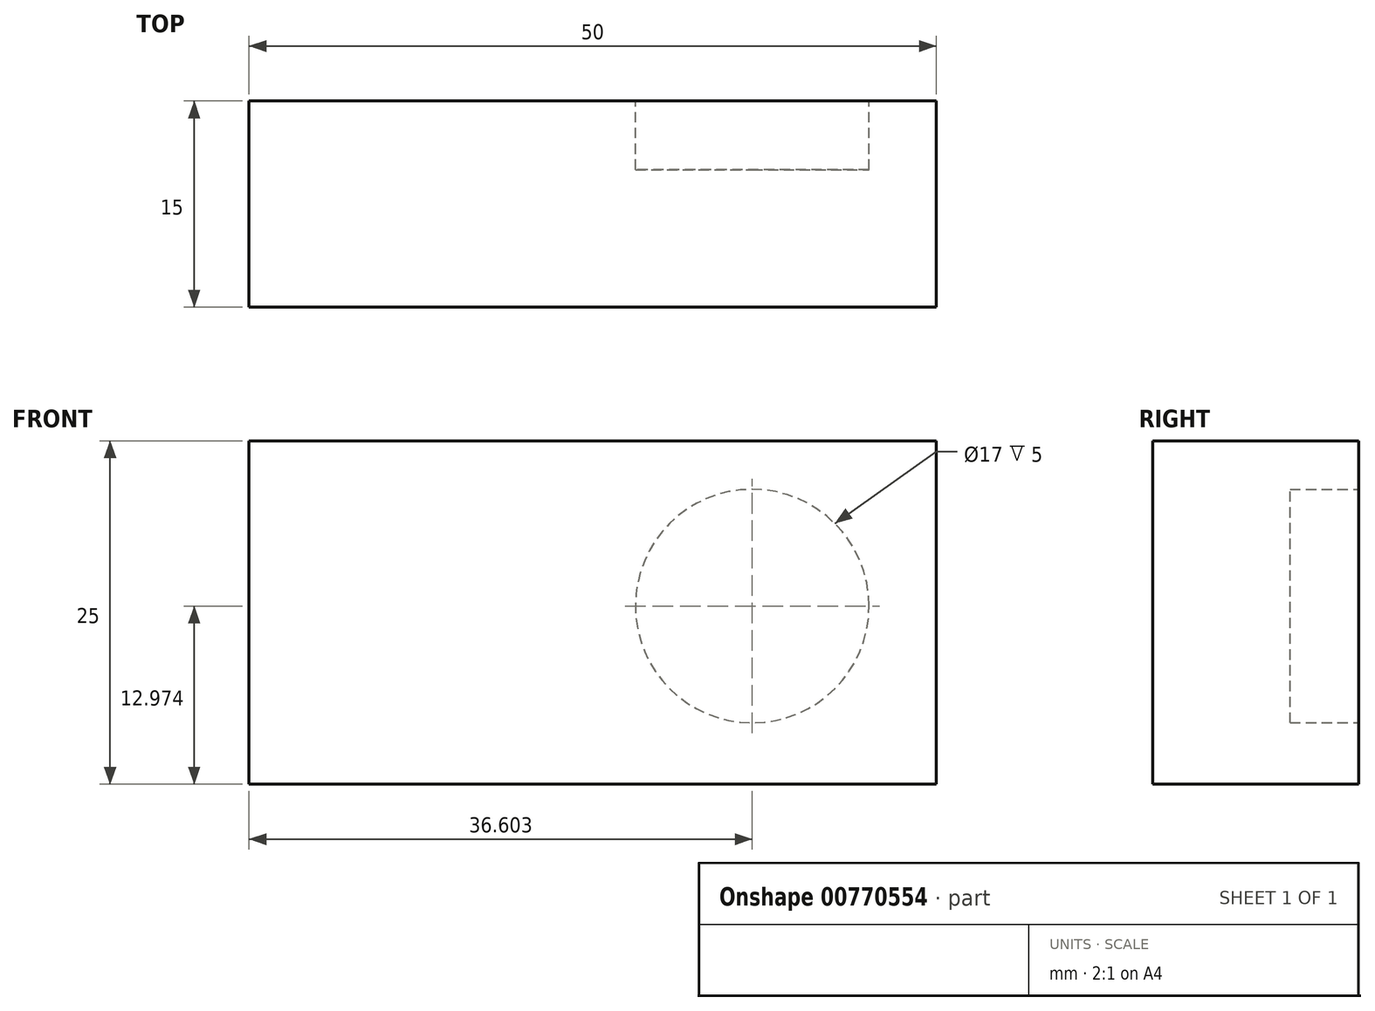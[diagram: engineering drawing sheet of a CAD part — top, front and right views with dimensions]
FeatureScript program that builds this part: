
annotation { "Feature Type Name" : "Feature", "Feature Type Description" : "" }
export const myFeature = defineFeature(function(context is Context, id is Id, definition is map)
    precondition{}
    {
        {
            var Q0;
            Q0=qCreatedBy(makeId("Front.planeOp"),FACE);
            var sketch = newSketch(context, id + "F0", { "sketchPlane" : qUnion([Q0])});
            skLineSegment(sketch, "E0.bottom", {"start": v(0, 0) * mm, "end": v(-50, 0) * mm});
            skLineSegment(sketch, "E0.top", {"start": v(0, 25) * mm, "end": v(-50, 25) * mm});
            skLineSegment(sketch, "E0.left", {"start": v(0, 0) * mm, "end": v(0, 25) * mm});
            skLineSegment(sketch, "E0.right", {"start": v(-50, 0) * mm, "end": v(-50, 25) * mm});
            skSolve(sketch);
        }
        {
            var Q0;
            Q0=qCreatedBy(makeId("Front.planeOp"),FACE);
            var sketch = newSketch(context, id + "F1", { "sketchPlane" : qUnion([Q0])});
            skCircle(sketch, "E1", {"center": v(-13.4, 12.97) * mm, "radius": 8.5 * mm});
            skSolve(sketch);
        }
        {
            var Q0;
            Q0 = qSketchRegion(id + "F0", true);
            extrude(context, id + "F2", {"entities" : qUnion([Q0]), "depth" : 15 * mm, "offsetDistance" : 25 * mm});
        }
        {
            var Q0;
            Q0 = qSketchRegion(id + "F1", true);
            extrude(context, id + "F3", {"entities" : qUnion([Q0]), "operationType" : NewBodyOperationType.REMOVE, "depth" : 5 * mm, "offsetDistance" : 25 * mm});
        }
    });
